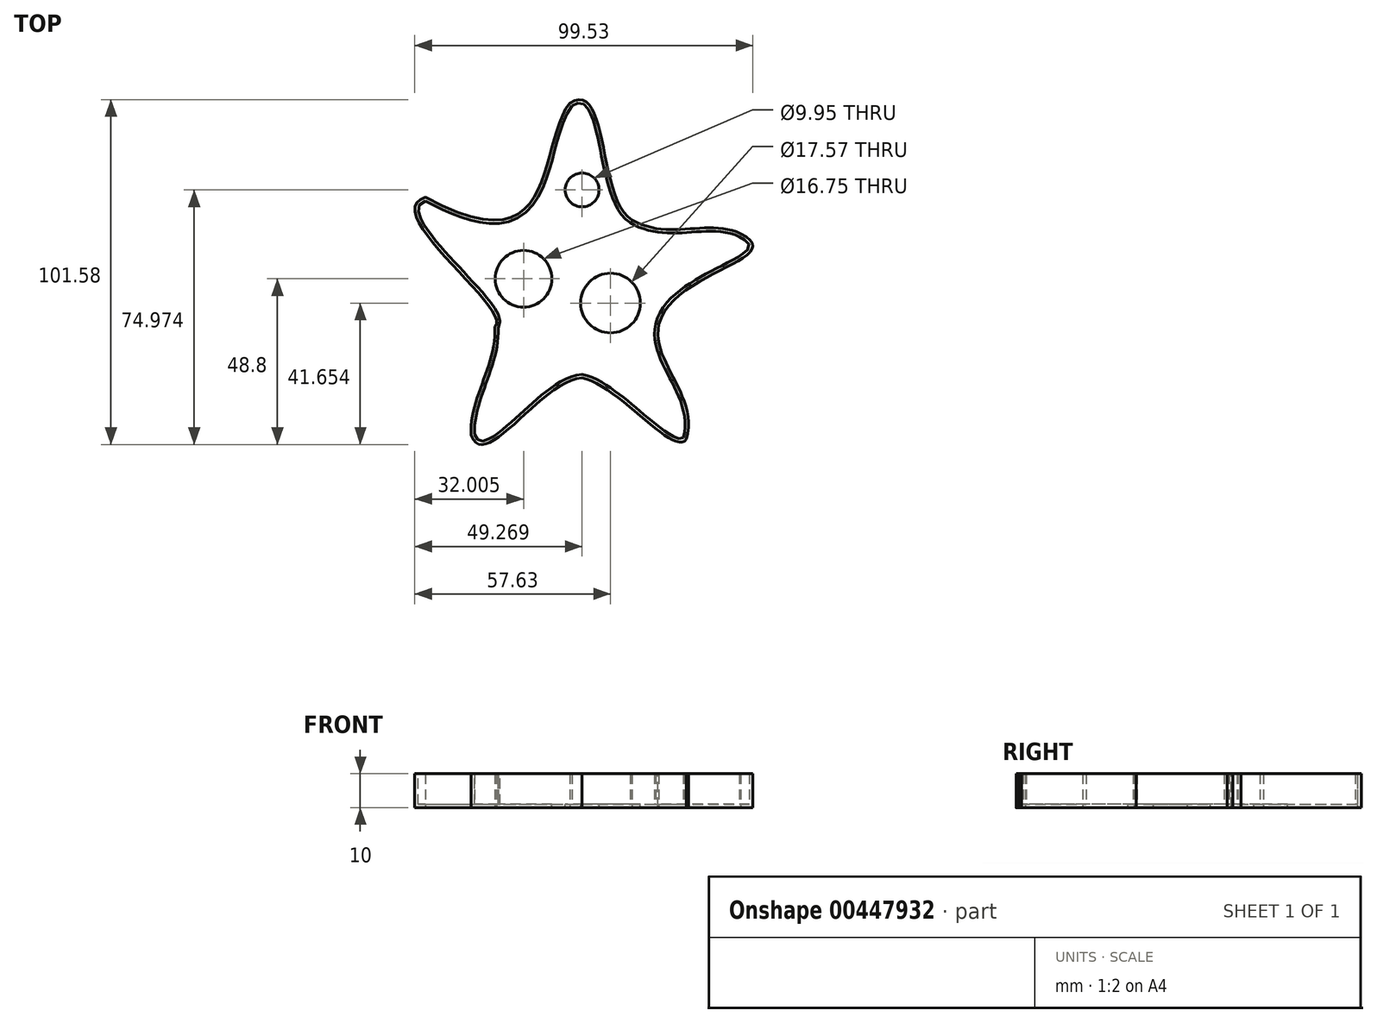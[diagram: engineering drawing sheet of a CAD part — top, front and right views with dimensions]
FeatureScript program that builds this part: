
annotation { "Feature Type Name" : "Feature", "Feature Type Description" : "" }
export const myFeature = defineFeature(function(context is Context, id is Id, definition is map)
    precondition{}
    {
        {
            var Q0;
            Q0=qCreatedBy(makeId("Top.planeOp"),FACE);
            var sketch = newSketch(context, id + "F0", { "sketchPlane" : qUnion([Q0])});
            skFitSpline(sketch, "E0", {"points": [v(-46.15, 20.93) * mm, v(-3.71, 48.64) * mm], "startDerivative": vector(119.47, -66.1) * mm, "endDerivative": vector(28.57, 35.8) * mm});
            skFitSpline(sketch, "E1", {"points": [v(-46.15, 20.93) * mm, v(-25.75, -17.17) * mm], "startDerivative": vector(-43.55, -13.02) * mm, "endDerivative": vector(-16.58, -15.71) * mm});
            skFitSpline(sketch, "E2", {"points": [v(-25.75, -17.17) * mm, v(-32.73, -49.17) * mm], "startDerivative": vector(1.75, -34.04) * mm, "endDerivative": vector(1.75, -32.3) * mm});
            skFitSpline(sketch, "E3", {"points": [v(-32.73, -49.17) * mm, v(-0.15, -32.3) * mm], "startDerivative": vector(12.22, -34.04) * mm, "endDerivative": vector(34.91, 1.75) * mm});
            skFitSpline(sketch, "E4", {"points": [v(14.7, 14.26) * mm, v(-3.71, 48.64) * mm], "startDerivative": vector(-31.42, 19.2) * mm, "endDerivative": vector(-35.14, -22.54) * mm});
            skFitSpline(sketch, "E5", {"points": [v(14.7, 14.26) * mm, v(46.7, 10.18) * mm], "startDerivative": vector(32.3, -19.2) * mm, "endDerivative": vector(29.68, -13.97) * mm});
            skFitSpline(sketch, "E6", {"points": [v(46.7, 10.18) * mm, v(22.55, -16.58) * mm], "startDerivative": vector(43.64, -22.7) * mm, "endDerivative": vector(-11.35, -47.13) * mm});
            skFitSpline(sketch, "E7", {"points": [v(22.55, -16.58) * mm, v(30.7, -50.33) * mm], "startDerivative": vector(-6.98, -34.04) * mm, "endDerivative": vector(-10.47, -40.15) * mm});
            skFitSpline(sketch, "E8", {"points": [v(-0.15, -32.3) * mm, v(30.7, -50.33) * mm], "startDerivative": vector(31.42, -5.24) * mm, "endDerivative": vector(11.35, 16.58) * mm});
            skSolve(sketch);
        }
        {
            var Q0;
            Q0 = qSketchRegion(id + "F0", true);
            extrude(context, id + "F1", {"entities" : qUnion([Q0]), "depth" : 10 * mm});
        }
        {
            var Q0;
            Q0=makeQuery(id+"F1.opExtrude","CAP_FACE",FACE,{"disambiguationData":[OSD([sQuery(id+"F0.wireOp",EDGE,"E0"),sQuery(id+"F0.wireOp",EDGE,"E1"),sQuery(id+"F0.wireOp",EDGE,"E2"),sQuery(id+"F0.wireOp",EDGE,"E3"),sQuery(id+"F0.wireOp",EDGE,"E4"),sQuery(id+"F0.wireOp",EDGE,"E5"),sQuery(id+"F0.wireOp",EDGE,"E6"),sQuery(id+"F0.wireOp",EDGE,"E7"),sQuery(id+"F0.wireOp",EDGE,"E8")])],"isStart":false});
            shell(context, id + "F2", {"entities" : qUnion([Q0]), "thickness" : 1 * mm});
        }
        {
            var Q0;
            Q0=makeQuery(id+"F2.opShell","OFFSET_FACE",FACE,{"disambiguationData":[OSD([sQuery(id+"F0.wireOp",EDGE,"E0"),sQuery(id+"F0.wireOp",EDGE,"E1"),sQuery(id+"F0.wireOp",EDGE,"E2"),sQuery(id+"F0.wireOp",EDGE,"E3"),sQuery(id+"F0.wireOp",EDGE,"E4"),sQuery(id+"F0.wireOp",EDGE,"E5"),sQuery(id+"F0.wireOp",EDGE,"E6"),sQuery(id+"F0.wireOp",EDGE,"E7"),sQuery(id+"F0.wireOp",EDGE,"E8")])]});
            var sketch = newSketch(context, id + "F3", { "sketchPlane" : qUnion([Q0])});
            skCircle(sketch, "E9", {"center": v(-0.04, 23.07) * mm, "radius": 5.82 * mm});
            skCircle(sketch, "E10", {"center": v(8.32, -10.25) * mm, "radius": 8.79 * mm});
            skCircle(sketch, "E11", {"center": v(-17.3, -3.1) * mm, "radius": 8.37 * mm});
            skCircle(sketch, "E12", {"center": v(-0.04, 23.07) * mm, "radius": 4.98 * mm});
            skSolve(sketch);
        }
        {
            var Q0;
            Q0=makeQuery(id+"F3.imprint","IMPRINT",FACE,{"disambiguationData":[TD([[makeQuery(id+"F3.imprint","IMPRINT",EDGE,{"derivedFrom":sQuery(id+"F3.wireOp",EDGE,"E11")}),1.0]])]});
            var Q1;
            Q1=makeQuery(id+"F3.imprint","IMPRINT",FACE,{"disambiguationData":[TD([[makeQuery(id+"F3.imprint","IMPRINT",EDGE,{"derivedFrom":sQuery(id+"F3.wireOp",EDGE,"E10")}),1.0]])]});
            var Q2;
            Q2=makeQuery(id+"F3.imprint","IMPRINT",FACE,{"disambiguationData":[TD([[makeQuery(id+"F3.imprint","IMPRINT",EDGE,{"derivedFrom":sQuery(id+"F3.wireOp",EDGE,"E12")}),1.0]])]});
            extrude(context, id + "F4", {"entities" : qUnion([Q0, Q1, Q2]), "operationType" : NewBodyOperationType.REMOVE, "oppositeDirection" : true, "depth" : 25 * mm});
        }
    });
